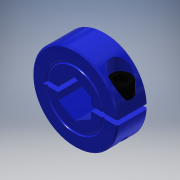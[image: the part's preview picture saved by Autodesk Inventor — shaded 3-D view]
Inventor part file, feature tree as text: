
AUTODESK INVENTOR PART (.ipt)
format: ipt  version: 2017.1 (Build 211199000, 199)  size: 293,376 bytes
history: native  units: in
note: dims shown in document units (in); Inventor stores cm internally (conversion verified against a paired STEP export)
features: extrude x2, sketch x2, other x1, imported_body x1
ambient origin geometry x8: Origin, YZ Plane, XZ Plane, XY Plane, X Axis, Y Axis, Z Axis, Center Point
bodies: Solid1 (feature_tree)
feature tree (6):
  other  "CL-8-A1"
  extrude  "Extrusion1"  Depth=0.4375in TaperAngle=0.0deg
  extrude  "Extrusion2"  [1 undecoded]
  imported_body  "Base1"
  sketch  "Sketch2"  dims[d0=0.5in d1=0.4375in d2=0.0in]
  sketch  "Sketch3"  dims[d3=1.0in d4=0.0in]
note: 1 required parameter value undecoded (feature->parameter linkage not recoverable at this tier; creation-order binding heuristic only, values carry confidence <= 0.55)
